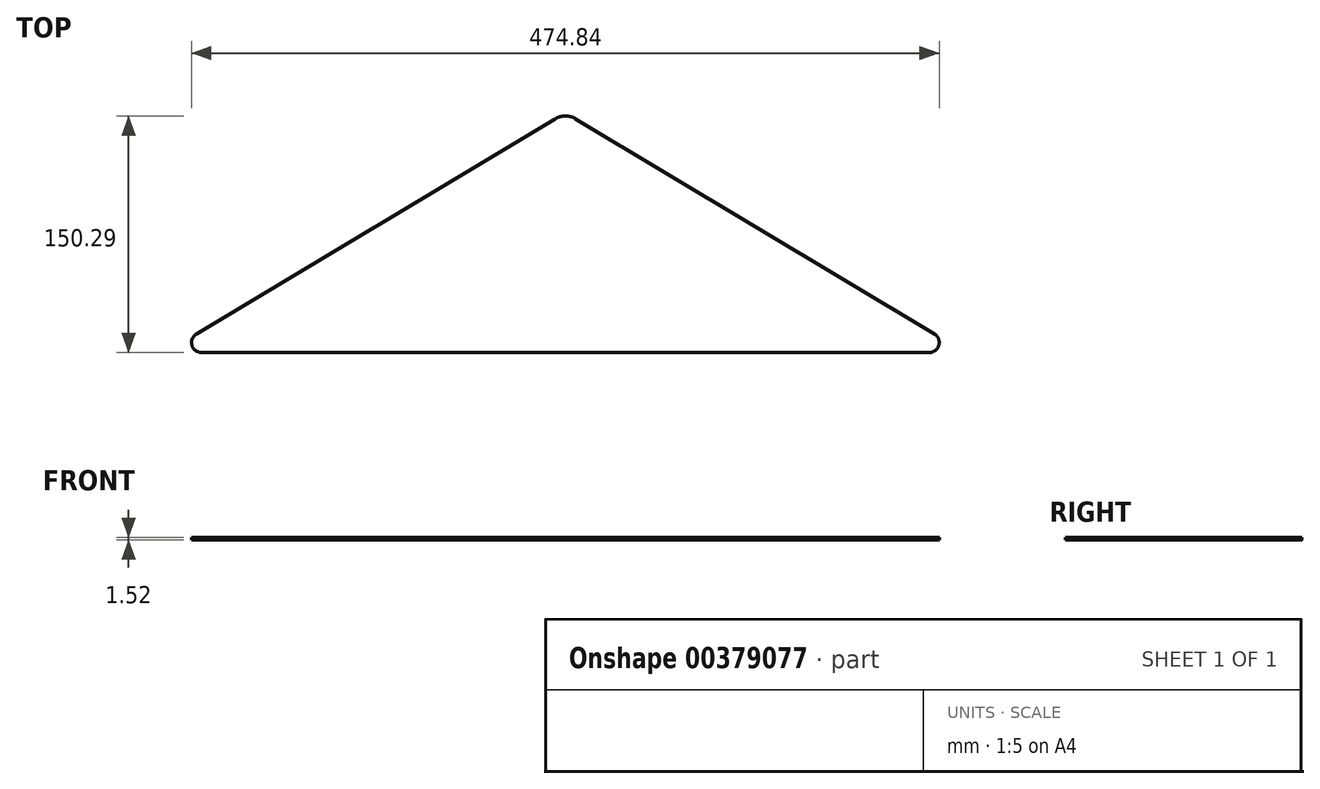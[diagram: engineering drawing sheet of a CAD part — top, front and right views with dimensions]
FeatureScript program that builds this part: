
annotation { "Feature Type Name" : "Feature", "Feature Type Description" : "" }
export const myFeature = defineFeature(function(context is Context, id is Id, definition is map)
    precondition{}
    {
        {
            var Q0;
            Q0=qCreatedBy(makeId("Top.planeOp"),FACE);
            var sketch = newSketch(context, id + "F0", { "sketchPlane" : qUnion([Q0])});
            skLineSegment(sketch, "E0", {"start": v(0, 0) * mm, "end": v(231.07, 0) * mm});
            skLineSegment(sketch, "E1", {"start": v(234.34, 11.8) * mm, "end": v(6.53, 148.48) * mm});
            skLineSegment(sketch, "E2", {"start": v(0, 152.4) * mm, "end": v(0, 0) * mm, "construction": true});
            skLineSegment(sketch, "E3.MirrorCS", {"start": v(-234.34, 11.8) * mm, "end": v(-6.53, 148.48) * mm});
            skLineSegment(sketch, "E4.MirrorCS", {"start": v(0, 0) * mm, "end": v(-231.07, 0) * mm});
            skPoint(sketch, "E5.visualSharp", {"position": v(0, 152.4) * mm});
            skArc(sketch, "E5.filletArc", {"start": v(6.53, 148.48) * mm, "mid": v(0, 150.29) * mm, "end": v(-6.53, 148.48) * mm});
            skPoint(sketch, "E6.visualSharp", {"position": v(-254, 0) * mm});
            skArc(sketch, "E6.filletArc", {"start": v(-234.34, 11.8) * mm, "mid": v(-237.2, 4.65) * mm, "end": v(-231.07, 0) * mm});
            skPoint(sketch, "E7.visualSharp", {"position": v(254, 0) * mm});
            skArc(sketch, "E7.filletArc", {"start": v(231.07, 0) * mm, "mid": v(237.2, 4.65) * mm, "end": v(234.34, 11.8) * mm});
            skSolve(sketch);
        }
        {
            var Q0;
            Q0=makeQuery(id+"F0.imprint","IMPRINT",FACE,{"disambiguationData":[TD([[makeQuery(id+"F0.imprint","IMPRINT",EDGE,{"derivedFrom":sQuery(id+"F0.wireOp",EDGE,"E0")}),1.0]])]});
            extrude(context, id + "F1", {"entities" : qUnion([Q0]), "depth" : 1.52 * mm});
        }
    });
